FCSTD DOCUMENT  (FreeCAD 0.19R24291 (Git))
Label: threading test
License: All rights reserved
LicenseURL: http://en.wikipedia.org/wiki/All_rights_reserved
objects: Sketcher::SketchObject×1, PartDesign::Body×1
note: 2 computed .brp shape members not serialized (recipe doc carries the construction recipe); baked Part::Feature solids carry a one-line shape summary decoded from their .brp

FEATURE [Sketcher::SketchObject] Sketch
  FullyConstrained = false
  MapMode = 5
  Support = -> [XY_Plane]
  sketch-geometry (4):
    g0: LineSegment StartX=-30.7785 StartY=20.8283 StartZ=0 EndX=30.7785 EndY=20.8283 EndZ=0
    g1: LineSegment StartX=30.7785 StartY=20.8283 StartZ=0 EndX=30.7785 EndY=-20.8283 EndZ=0
    g2: LineSegment StartX=30.7785 StartY=-20.8283 StartZ=0 EndX=-30.7785 EndY=-20.8283 EndZ=0
    g3: LineSegment StartX=-30.7785 StartY=-20.8283 StartZ=0 EndX=-30.7785 EndY=20.8283 EndZ=0
  constraints (9):
    c: Coincident(g0,g1)
    c: Coincident(g1,g2)
    c: Coincident(g2,g3)
    c: Coincident(g3,g0)
    c: Horizontal(g0)
    c: Horizontal(g2)
    c: Vertical(g1)
    c: Vertical(g3)
    c: Symmetric(g0,g1,g-1)
FEATURE [PartDesign::Body] Body
  Group = -> [Sketch]
  Origin = -> Origin
